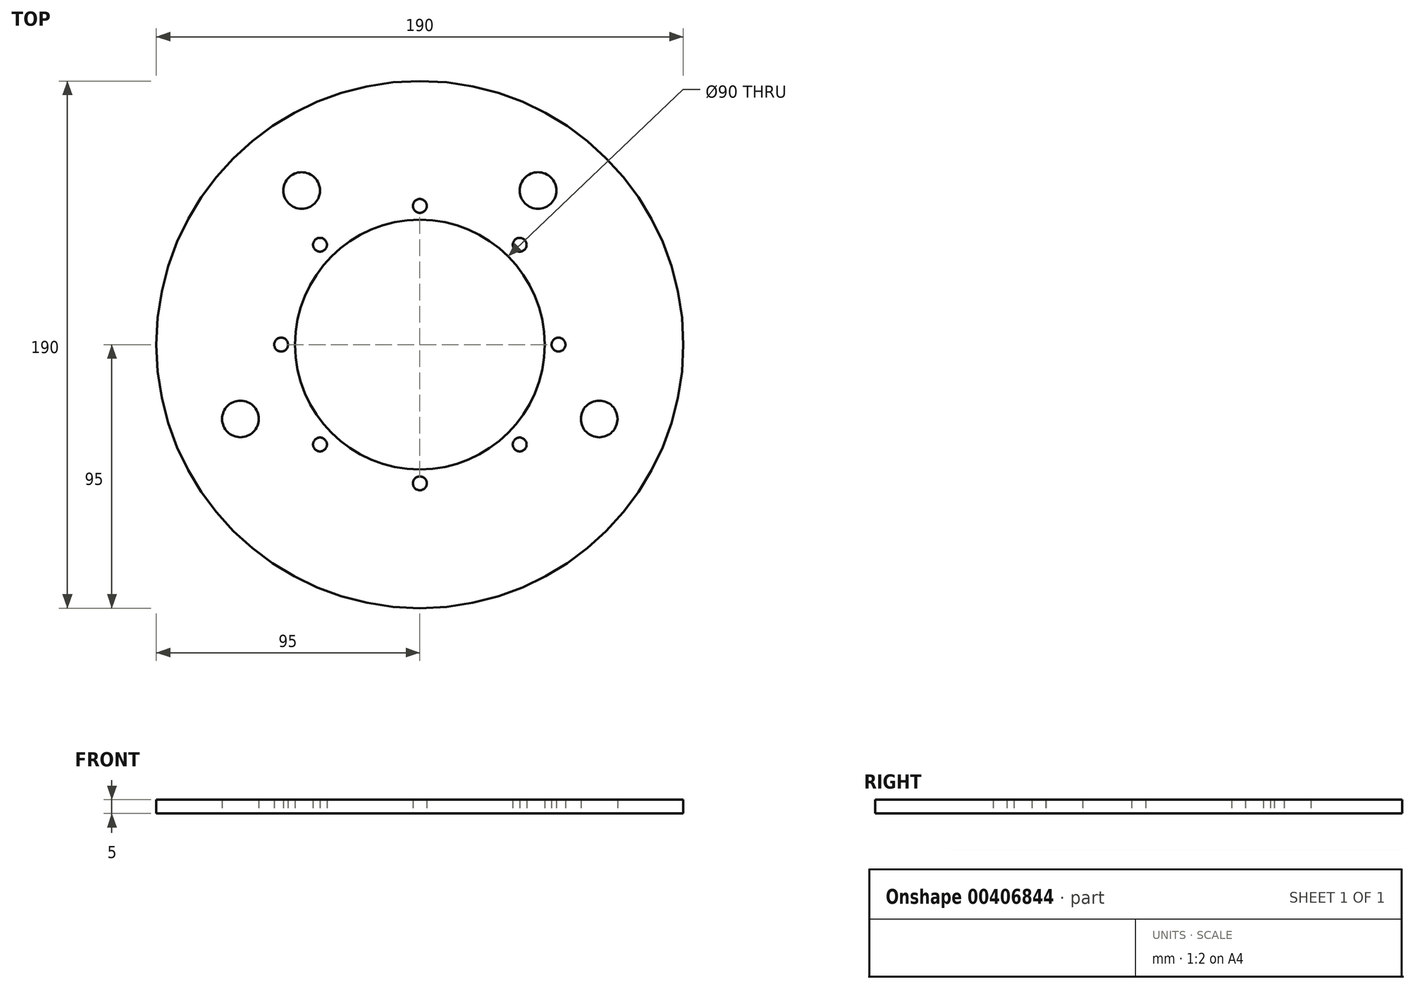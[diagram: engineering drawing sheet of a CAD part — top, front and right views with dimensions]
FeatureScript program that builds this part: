
annotation { "Feature Type Name" : "Feature", "Feature Type Description" : "" }
export const myFeature = defineFeature(function(context is Context, id is Id, definition is map)
    precondition{}
    {
        {
            var Q0;
            Q0=qCreatedBy(makeId("Top.planeOp"),FACE);
            var sketch = newSketch(context, id + "F0", { "sketchPlane" : qUnion([Q0])});
            skPoint(sketch, "E0.middle", {"position": v(0, 0) * mm});
            skCircle(sketch, "E1", {"center": v(0, 0) * mm, "radius": 95 * mm});
            skCircle(sketch, "E2", {"center": v(-36, 36) * mm, "radius": 2.5 * mm});
            skCircle(sketch, "E3.1.0", {"center": v(-36, -36) * mm, "radius": 2.5 * mm});
            skCircle(sketch, "E3.2.0", {"center": v(36, -36) * mm, "radius": 2.5 * mm});
            skCircle(sketch, "E3.3.0", {"center": v(36, 36) * mm, "radius": 2.5 * mm});
            skCircle(sketch, "E4", {"center": v(-50, 0) * mm, "radius": 2.5 * mm});
            skCircle(sketch, "E5.1.0", {"center": v(0, -50) * mm, "radius": 2.5 * mm});
            skCircle(sketch, "E5.2.0", {"center": v(50, 0) * mm, "radius": 2.5 * mm});
            skCircle(sketch, "E5.3.0", {"center": v(0, 50) * mm, "radius": 2.5 * mm});
            skCircle(sketch, "E6", {"center": v(0, 0) * mm, "radius": 45 * mm});
            skCircle(sketch, "E7", {"center": v(-64.67, -26.79) * mm, "radius": 6.6 * mm});
            skLineSegment(sketch, "E8", {"start": v(-64.67, -26.79) * mm, "end": v(0, 0) * mm, "construction": true});
            skCircle(sketch, "E9.1.0", {"center": v(-42.61, 55.53) * mm, "radius": 6.6 * mm});
            skCircle(sketch, "E9.2.0", {"center": v(42.61, 55.53) * mm, "radius": 6.6 * mm});
            skCircle(sketch, "E9.3.0", {"center": v(64.67, -26.79) * mm, "radius": 6.6 * mm});
            skLineSegment(sketch, "E9.anchor1", {"start": v(0, 0) * mm, "end": v(-64.67, -26.79) * mm, "construction": true});
            skLineSegment(sketch, "E9.anchor2", {"start": v(0, 0) * mm, "end": v(64.67, -26.79) * mm, "construction": true});
            skSolve(sketch);
        }
        {
            var Q0;
            Q0 = qSketchRegion(id + "F0", true);
            extrude(context, id + "F1", {"entities" : qUnion([Q0]), "depth" : 5 * mm});
        }
    });
